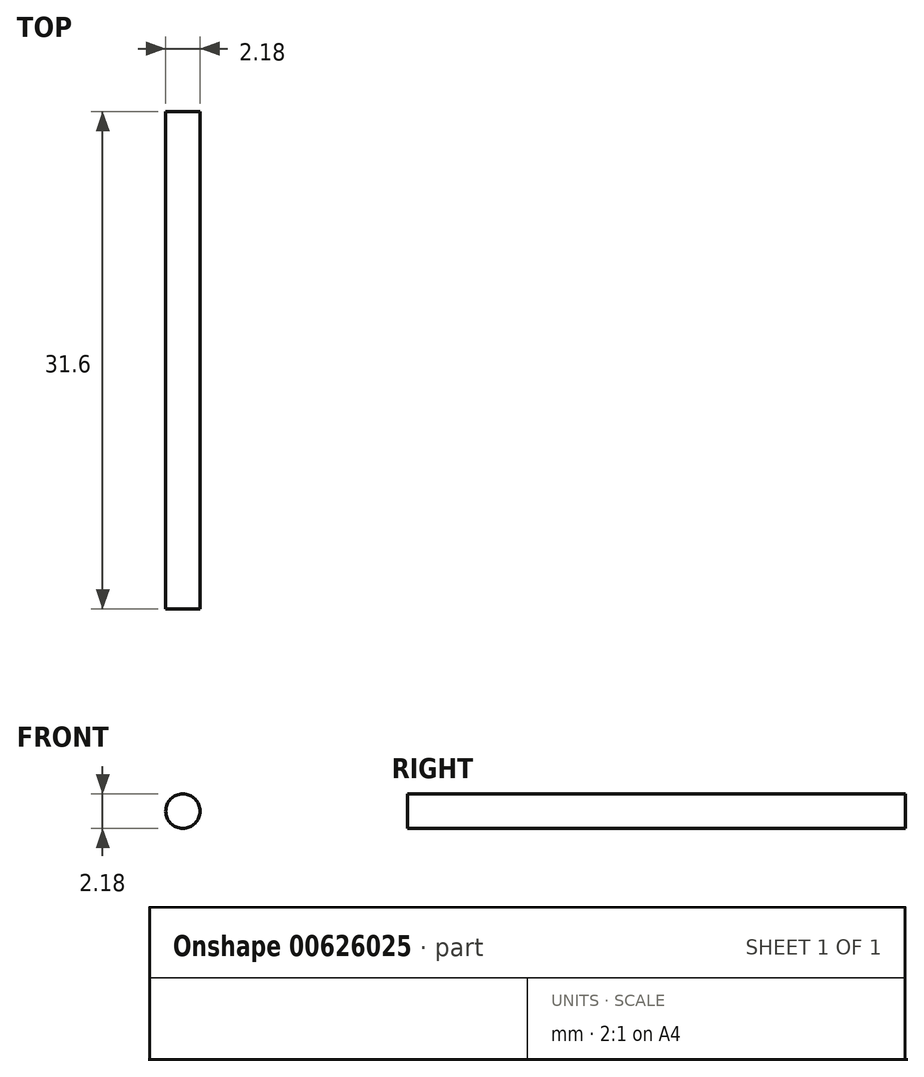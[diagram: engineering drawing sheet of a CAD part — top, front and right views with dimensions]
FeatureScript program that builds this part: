
annotation { "Feature Type Name" : "Feature", "Feature Type Description" : "" }
export const myFeature = defineFeature(function(context is Context, id is Id, definition is map)
    precondition{}
    {
        {
            var Q0;
            Q0=qCreatedBy(makeId("Front.planeOp"),FACE);
            var sketch = newSketch(context, id + "F0", { "sketchPlane" : qUnion([Q0])});
            skCircle(sketch, "E0", {"center": v(0, 0) * mm, "radius": 1.09 * mm});
            skSolve(sketch);
        }
        {
            var Q0;
            Q0 = qSketchRegion(id + "F0", true);
            extrude(context, id + "F1", {"entities" : qUnion([Q0]), "depth" : 31.6 * mm, "offsetDistance" : 25 * mm});
        }
    });
